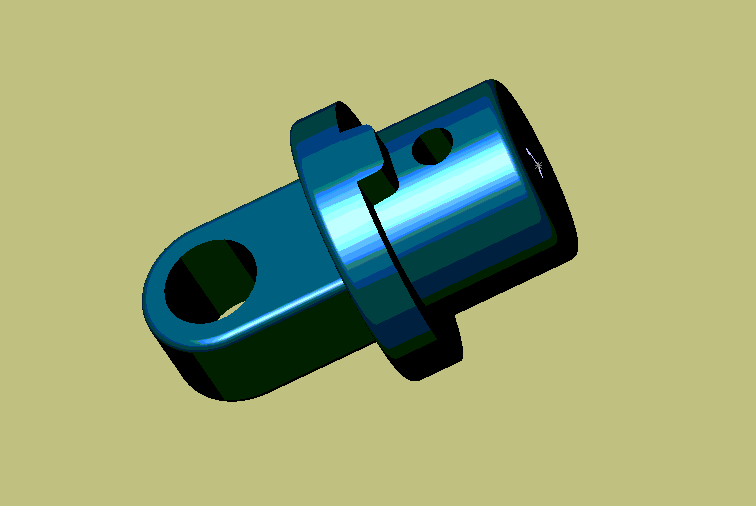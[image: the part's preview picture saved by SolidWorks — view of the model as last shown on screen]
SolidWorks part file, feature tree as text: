
SOLIDWORKS PART (.sldprt)
format: sldprt  version: not decoded by parser v0  size: 227,840 bytes
history: native  units: mm
features: sketch x5, extrude x4, plane x3, material x1, cut_extrude x1, fillet x1 (+8 scaffold rows collapsed)
feature tree (23):
  scaffold x8  (default folders/planes/origin — collapsed)
  material  "Matériau <non spécifié>"
  plane  "Plane1"
  plane  "Plane2"
  plane  "Plane3"
  sketch  "Esquisse1"  dims[D1=9.0mm]
  extrude  "Base-Extrusion"  Depth=7mm
  sketch  "Esquisse2"  dims[D1=13.0mm]
  extrude  "Boss.-Extru.1"  Depth=2.5mm
  sketch  "Esquisse3"  dims[D1=3.5mm D2=6.0mm D3=6.0mm]
  extrude  "Boss.-Extru.2"  Depth=5mm
  sketch  "Esquisse4"  dims[c1.D1=4.5mm c1.D2=12.5mm c2.D2=90.0deg c2.D3=3.5mm]
  cut_extrude  "Enlèv. mat.-Extru.1"  Depth=45mm
  sketch  "Esquisse5"  dims[D2=6.5mm D1=3.0mm]
  extrude  "Boss.-Extru.3"  Depth=1.5mm
  fillet  "Congé1"  Radius=0.5mm
decode coverage: 11 of 11 modeling features carry decoded parameters
note: suppression state not decoded; provenance and decode notes live in map.json
